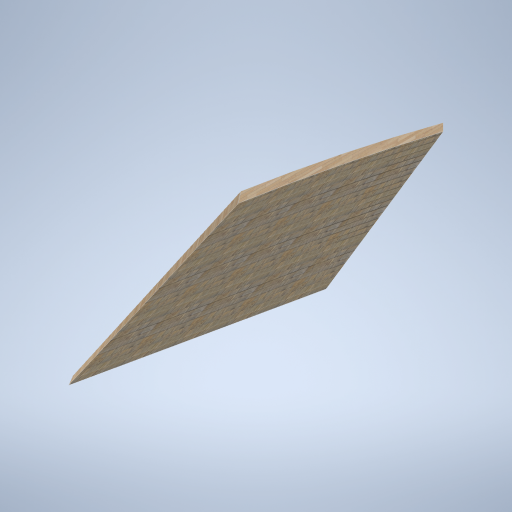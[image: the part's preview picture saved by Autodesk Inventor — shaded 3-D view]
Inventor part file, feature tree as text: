
AUTODESK INVENTOR PART (.ipt)
format: ipt  version: 2024.2 (Build 282272000, 272)  size: 336,896 bytes
history: native  units: mm
features: sketch x3, plane x2, loft x1
ambient origin geometry x8: Origin, YZ Plane, XZ Plane, XY Plane, X Axis, Y Axis, Z Axis, Center Point
bodies: Body1 (feature_tree)
feature tree (6):
  sketch  "Sketch6"  dims[d10=0.0mm d11=1791.0mm d13=0.0mm d14=90.0deg]
  plane  "Work Plane4"
  loft  "Loft3"
  plane  "Work Plane3"
  sketch  "Sketch7"  dims[d15=0.0mm d16=90.0deg]
  sketch  "Sketch8"  dims[d17=50000.0mm]
